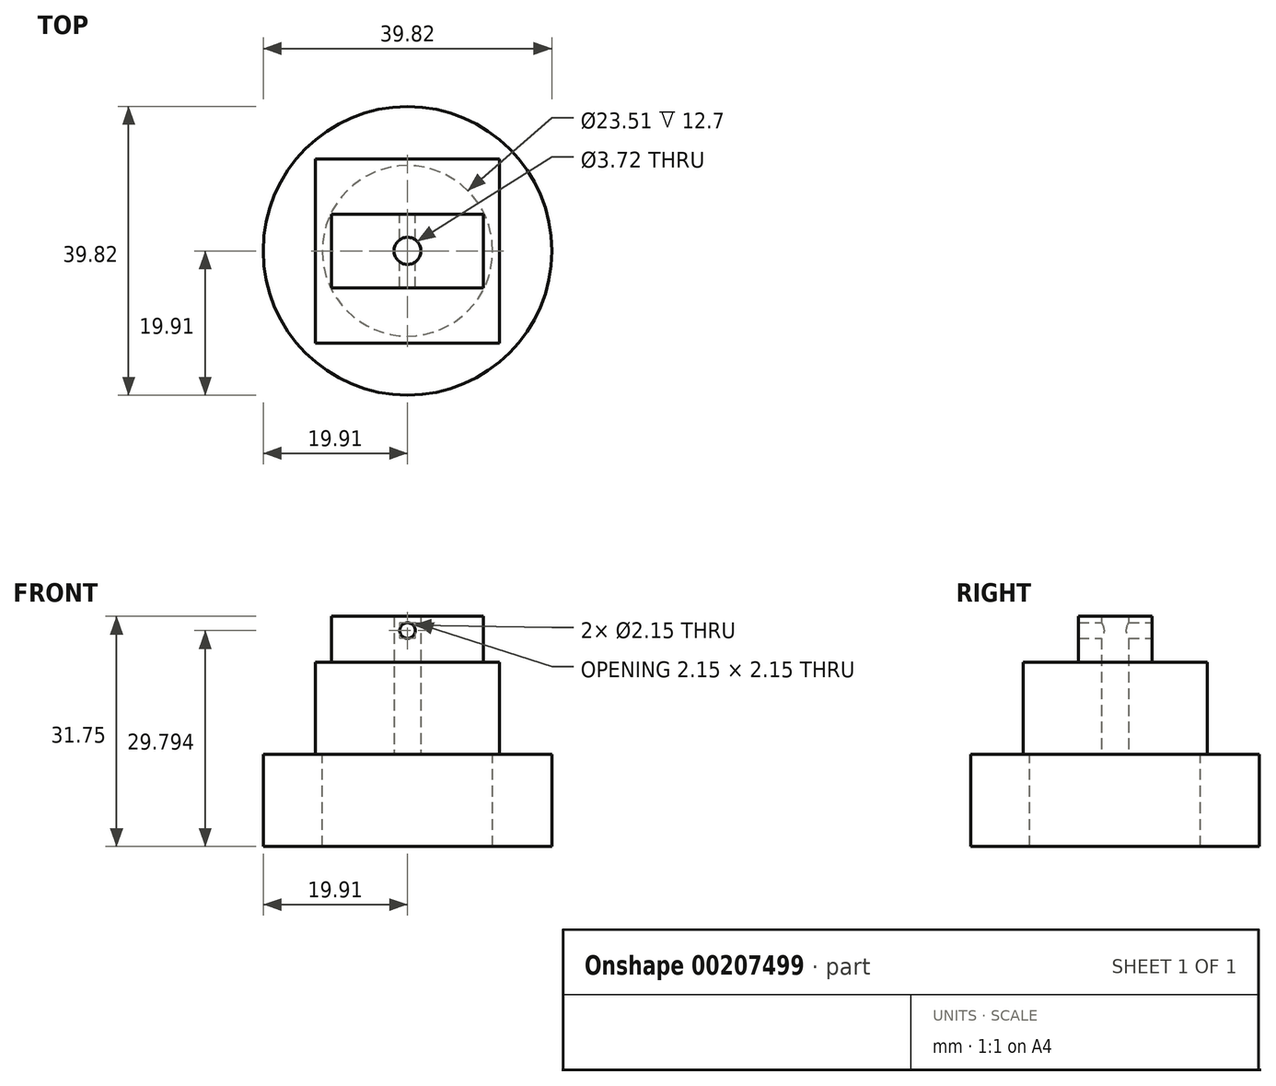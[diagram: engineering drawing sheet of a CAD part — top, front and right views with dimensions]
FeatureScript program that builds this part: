
annotation { "Feature Type Name" : "Feature", "Feature Type Description" : "" }
export const myFeature = defineFeature(function(context is Context, id is Id, definition is map)
    precondition{}
    {
        {
            var Q0;
            Q0=qCreatedBy(makeId("Top.planeOp"),FACE);
            var sketch = newSketch(context, id + "F0", { "sketchPlane" : qUnion([Q0])});
            skCircle(sketch, "E0", {"center": v(0, 0) * mm, "radius": 11.75 * mm});
            skSolve(sketch);
        }
        {
            var Q0;
            Q0=qCreatedBy(makeId("Top.planeOp"),FACE);
            var sketch = newSketch(context, id + "F1", { "sketchPlane" : qUnion([Q0])});
            skCircle(sketch, "E1", {"center": v(0, 0) * mm, "radius": 19.9 * mm});
            skSolve(sketch);
        }
        {
            var Q0;
            Q0=qSketchRegion(id+"F1",true);
            extrude(context, id + "F2", {"entities" : qUnion([Q0]), "oppositeDirection" : true, "depth" : 12.7 * mm});
        }
        {
            var Q0;
            Q0=qSketchRegion(id+"F0",true);
            extrude(context, id + "F3", {"entities" : qUnion([Q0]), "operationType" : NewBodyOperationType.REMOVE, "oppositeDirection" : true, "depth" : 12.7 * mm});
        }
        {
            var Q0;
            Q0=qCreatedBy(makeId("Top.planeOp"),FACE);
            var sketch = newSketch(context, id + "F4", { "sketchPlane" : qUnion([Q0])});
            skLineSegment(sketch, "E2.bottom", {"start": v(12.7, -12.7) * mm, "end": v(-12.7, -12.7) * mm});
            skLineSegment(sketch, "E2.top", {"start": v(12.7, 12.7) * mm, "end": v(-12.7, 12.7) * mm});
            skLineSegment(sketch, "E2.left", {"start": v(12.7, -12.7) * mm, "end": v(12.7, 12.7) * mm});
            skLineSegment(sketch, "E2.right", {"start": v(-12.7, -12.7) * mm, "end": v(-12.7, 12.7) * mm});
            skPoint(sketch, "E2.middle", {"position": v(0, 0) * mm});
            skSolve(sketch);
        }
        {
            var Q0;
            Q0 = qSketchRegion(id + "F4", true);
            extrude(context, id + "F5", {"entities" : qUnion([Q0]), "operationType" : NewBodyOperationType.ADD, "depth" : 12.7 * mm});
        }
        {
            var Q0;
            Q0=qCreatedBy(makeId("Top.planeOp"),FACE);
            var sketch = newSketch(context, id + "F6", { "sketchPlane" : qUnion([Q0])});
            skLineSegment(sketch, "E3.bottom", {"start": v(10.48, -5.08) * mm, "end": v(-10.48, -5.08) * mm});
            skLineSegment(sketch, "E3.top", {"start": v(10.48, 5.08) * mm, "end": v(-10.48, 5.08) * mm});
            skLineSegment(sketch, "E3.left", {"start": v(10.48, -5.08) * mm, "end": v(10.48, 5.08) * mm});
            skLineSegment(sketch, "E3.right", {"start": v(-10.48, -5.08) * mm, "end": v(-10.48, 5.08) * mm});
            skPoint(sketch, "E3.middle", {"position": v(0, 0) * mm});
            skSolve(sketch);
        }
        {
            var Q0;
            Q0 = qSketchRegion(id + "F6", true);
            extrude(context, id + "F7", {"entities" : qUnion([Q0]), "operationType" : NewBodyOperationType.ADD, "depth" : 19.05 * mm});
        }
        {
            var Q0;
            Q0=qCreatedBy(makeId("Front.planeOp"),FACE);
            var sketch = newSketch(context, id + "F8", { "sketchPlane" : qUnion([Q0])});
            skCircle(sketch, "E4", {"center": v(0, 17.1) * mm, "radius": 1.08 * mm});
            skSolve(sketch);
        }
        {
            var Q0;
            Q0 = qSketchRegion(id + "F8", true);
            extrude(context, id + "F9", {"entities" : qUnion([Q0]), "operationType" : NewBodyOperationType.REMOVE, "endBound" : BoundingType.SYMMETRIC, "depth" : 11.43 * mm});
        }
        {
            var Q0;
            Q0=qCreatedBy(makeId("Top.planeOp"),FACE);
            var sketch = newSketch(context, id + "F10", { "sketchPlane" : qUnion([Q0])});
            skCircle(sketch, "E5", {"center": v(0, 0) * mm, "radius": 1.86 * mm});
            skSolve(sketch);
        }
        {
            var Q0;
            Q0 = qSketchRegion(id + "F10", true);
            extrude(context, id + "F11", {"entities" : qUnion([Q0]), "operationType" : NewBodyOperationType.REMOVE, "depth" : 19.05 * mm});
        }
    });
